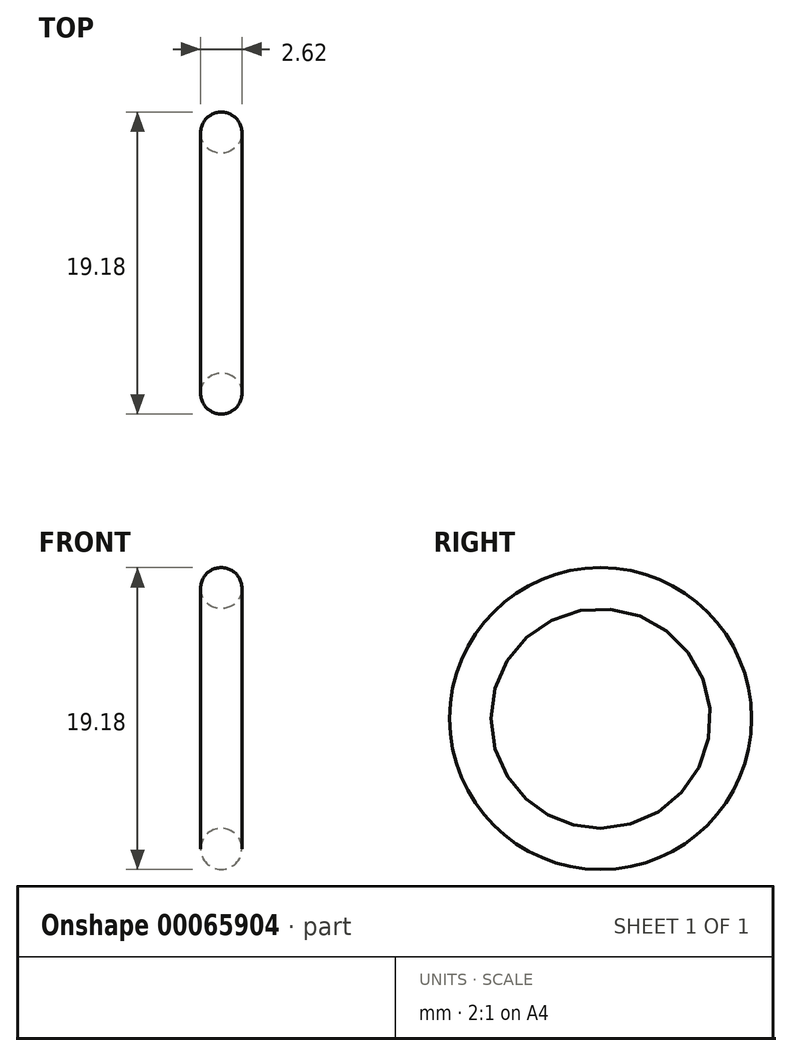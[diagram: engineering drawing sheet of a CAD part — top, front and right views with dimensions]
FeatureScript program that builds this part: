
annotation { "Feature Type Name" : "Feature", "Feature Type Description" : "" }
export const myFeature = defineFeature(function(context is Context, id is Id, definition is map)
    precondition{}
    {
        {
            var Q0;
            Q0=qCreatedBy(makeId("Front.planeOp"),FACE);
            var sketch = newSketch(context, id + "F0", { "sketchPlane" : qUnion([Q0])});
            skLineSegment(sketch, "E0", {"start": v(0, 0) * mm, "end": v(-6.06, 0) * mm, "construction": true});
            skCircle(sketch, "E1", {"center": v(0, 8.28) * mm, "radius": 1.3 * mm});
            skSolve(sketch);
        }
        {
            var Q0;
            Q0=makeQuery(id+"F0.imprint","IMPRINT",FACE,{"disambiguationData":[TD([[makeQuery(id+"F0.imprint","IMPRINT",EDGE,{"derivedFrom":sQuery(id+"F0.wireOp",EDGE,"E1")}),1.0]])]});
            var Q1;
            Q1=sQuery(id+"F0.wireOp",EDGE,"E0");
            revolve(context, id + "F1", {"entities" : qUnion([Q0]), "axis" : qUnion([Q1]), "revolveType" : RevolveType.FULL});
        }
    });
